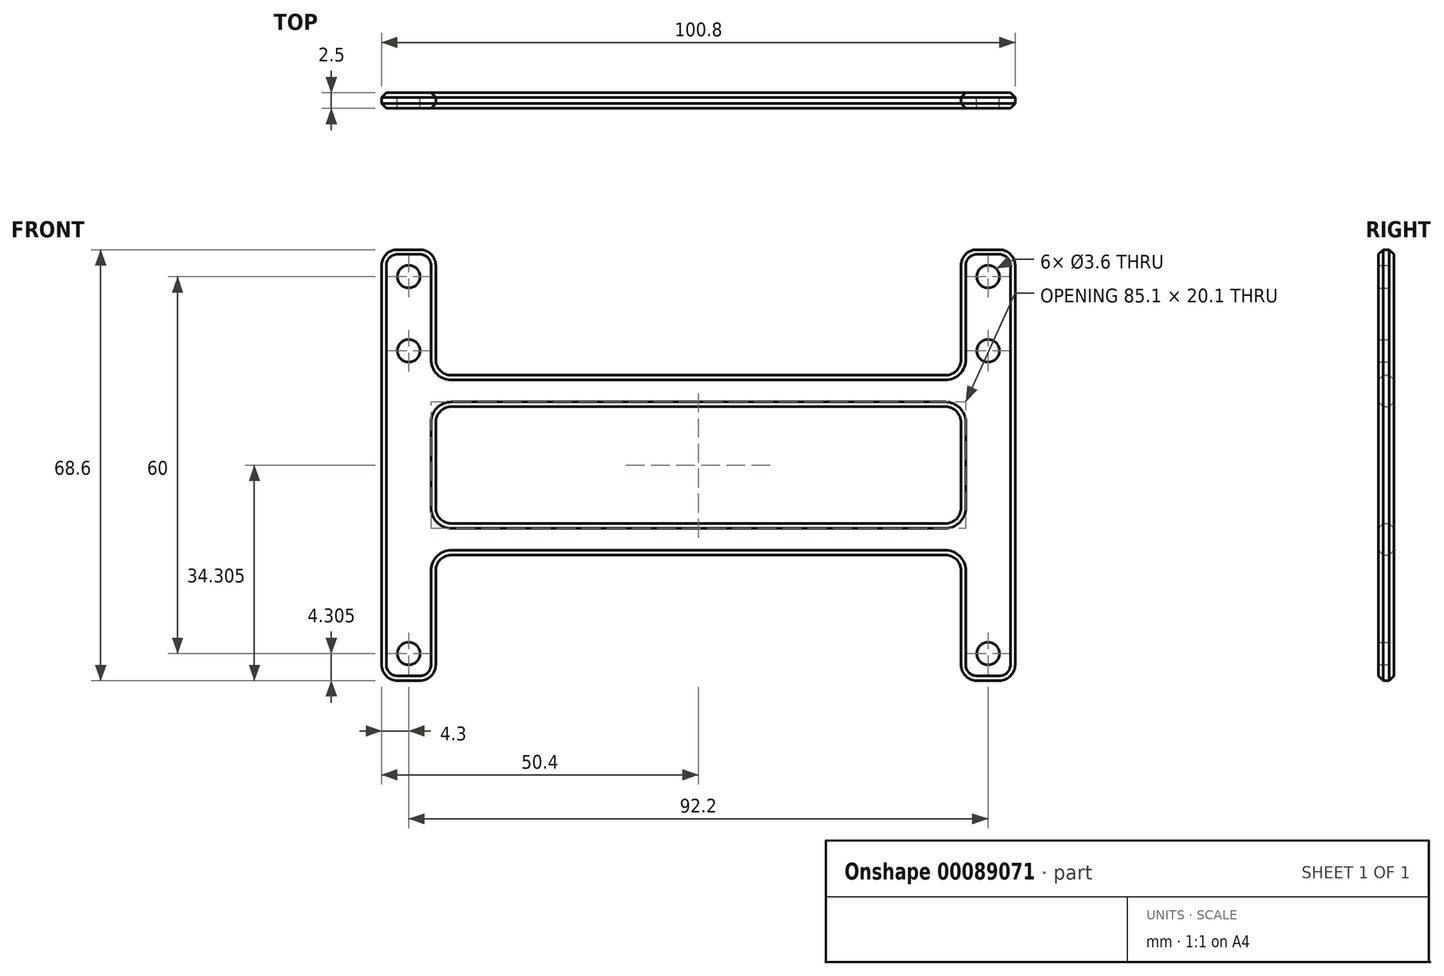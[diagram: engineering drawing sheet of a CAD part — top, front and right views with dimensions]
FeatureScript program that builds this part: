
annotation { "Feature Type Name" : "Feature", "Feature Type Description" : "" }
export const myFeature = defineFeature(function(context is Context, id is Id, definition is map)
    precondition{}
    {
        {
            var Q0;
            Q0=qCreatedBy(makeId("Front.planeOp"),FACE);
            var sketch = newSketch(context, id + "F0", { "sketchPlane" : qUnion([Q0])});
            skLineSegment(sketch, "E0.bottom", {"start": v(-50.4, 64.62) * mm, "end": v(-41.8, 64.62) * mm});
            skLineSegment(sketch, "E0.top", {"start": v(-50.4, -3.98) * mm, "end": v(-41.8, -3.98) * mm});
            skLineSegment(sketch, "E0.left", {"start": v(-50.4, 64.62) * mm, "end": v(-50.4, -3.98) * mm});
            skLineSegment(sketch, "E1", {"start": v(-46.1, 64.62) * mm, "end": v(-46.1, -55.68) * mm, "construction": true});
            skCircle(sketch, "E2", {"center": v(-46.1, 60.32) * mm, "radius": 1.8 * mm});
            skCircle(sketch, "E3", {"center": v(-46.1, 48.52) * mm, "radius": 1.8 * mm});
            skCircle(sketch, "E4", {"center": v(-46.1, 0.32) * mm, "radius": 1.8 * mm});
            skLineSegment(sketch, "E5", {"start": v(-41.8, 64.62) * mm, "end": v(-41.8, -3.98) * mm});
            skLineSegment(sketch, "E6.bottom", {"start": v(-41.8, 44.62) * mm, "end": v(0, 44.62) * mm});
            skLineSegment(sketch, "E6.top", {"start": v(-41.8, 39.62) * mm, "end": v(0, 39.62) * mm});
            skLineSegment(sketch, "E6.left", {"start": v(-41.8, 44.62) * mm, "end": v(-41.8, 39.62) * mm});
            skLineSegment(sketch, "E6.right", {"start": v(0, 44.62) * mm, "end": v(0, 39.62) * mm});
            skLineSegment(sketch, "E7.bottom", {"start": v(-41.83, 21.03) * mm, "end": v(0, 21.02) * mm});
            skLineSegment(sketch, "E7.top", {"start": v(-41.83, 16.03) * mm, "end": v(0, 16.02) * mm});
            skLineSegment(sketch, "E7.left", {"start": v(-41.83, 21.03) * mm, "end": v(-41.83, 16.03) * mm});
            skLineSegment(sketch, "E7.right", {"start": v(0, 21.02) * mm, "end": v(0, 16.02) * mm});
            skLineSegment(sketch, "E8.MirrorCS", {"start": v(41.83, 21.03) * mm, "end": v(41.83, 16.03) * mm});
            skCircle(sketch, "E9.MirrorC", {"center": v(46.1, 48.52) * mm, "radius": 1.8 * mm});
            skLineSegment(sketch, "E10.MirrorCS", {"start": v(41.8, 44.62) * mm, "end": v(41.8, 39.62) * mm});
            skLineSegment(sketch, "E11.MirrorCS", {"start": v(41.83, 16.02) * mm, "end": v(0, 16.02) * mm});
            skLineSegment(sketch, "E12.MirrorCS", {"start": v(41.83, 21.02) * mm, "end": v(0, 21.02) * mm});
            skCircle(sketch, "E13.MirrorC", {"center": v(46.1, 0.32) * mm, "radius": 1.8 * mm});
            skCircle(sketch, "E14.MirrorC", {"center": v(46.1, 60.32) * mm, "radius": 1.8 * mm});
            skLineSegment(sketch, "E15.MirrorCS", {"start": v(41.8, 39.62) * mm, "end": v(0, 39.62) * mm});
            skLineSegment(sketch, "E16.MirrorCS", {"start": v(50.4, 64.62) * mm, "end": v(50.4, -3.98) * mm});
            skLineSegment(sketch, "E17.MirrorCS", {"start": v(50.4, -3.98) * mm, "end": v(41.8, -3.98) * mm});
            skLineSegment(sketch, "E18.MirrorCS", {"start": v(41.8, 64.62) * mm, "end": v(41.8, -3.98) * mm});
            skLineSegment(sketch, "E19.MirrorCS", {"start": v(50.4, 64.62) * mm, "end": v(41.8, 64.62) * mm});
            skLineSegment(sketch, "E20.MirrorCS", {"start": v(41.8, 44.62) * mm, "end": v(0, 44.62) * mm});
            skSolve(sketch);
        }
        {
            var Q0;
            {var subQ5=sQuery(id+"F0.wireOp",EDGE,"E7.left");Q0=makeQuery(id+"F0.imprint","IMPRINT",FACE,{"disambiguationData":[TD([[makeQuery(id+"F0.imprint","IMPRINT",EDGE,{"derivedFrom":subQ5}),1.0]])]});}
            var Q1;
            {var subQ0=sQuery(id+"F0.wireOp",EDGE,"E8.MirrorCS");Q1=makeQuery(id+"F0.imprint","IMPRINT",FACE,{"disambiguationData":[TD([[makeQuery(id+"F0.imprint","IMPRINT",EDGE,{"derivedFrom":subQ0}),-1.0]])]});}
            var Q2;
            {var subQ5=sQuery(id+"F0.wireOp",EDGE,"E7.right");Q2=makeQuery(id+"F0.imprint","IMPRINT",FACE,{"disambiguationData":[TD([[makeQuery(id+"F0.imprint","IMPRINT",EDGE,{"derivedFrom":subQ5}),-1.0]])]});}
            var Q3;
            {var subQ0=sQuery(id+"F0.wireOp",EDGE,"E7.right");Q3=makeQuery(id+"F0.imprint","IMPRINT",FACE,{"disambiguationData":[TD([[makeQuery(id+"F0.imprint","IMPRINT",EDGE,{"derivedFrom":subQ0}),1.0]])]});}
            var Q4;
            {var subQ0=sQuery(id+"F0.wireOp",EDGE,"E15.MirrorCS");Q4=makeQuery(id+"F0.imprint","IMPRINT",FACE,{"disambiguationData":[TD([[makeQuery(id+"F0.imprint","IMPRINT",EDGE,{"derivedFrom":subQ0}),-1.0]])]});}
            var Q5;
            {var subQ9=sQuery(id+"F0.wireOp",EDGE,"E8.MirrorCS");Q5=makeQuery(id+"F0.imprint","IMPRINT",FACE,{"disambiguationData":[TD([[makeQuery(id+"F0.imprint","IMPRINT",EDGE,{"derivedFrom":subQ9}),1.0]])]});}
            var Q6;
            Q6=makeQuery(id+"F0.imprint","IMPRINT",FACE,{"disambiguationData":[TD([[makeQuery(id+"F0.imprint","IMPRINT",EDGE,{"derivedFrom":sQuery(id+"F0.wireOp",EDGE,"E6.bottom")}),-1.0]])]});
            var Q7;
            Q7=makeQuery(id+"F0.imprint","IMPRINT",FACE,{"disambiguationData":[TD([[makeQuery(id+"F0.imprint","IMPRINT",EDGE,{"derivedFrom":sQuery(id+"F0.wireOp",EDGE,"6060c022-7060-453b-8efb-dcd9e4211910.sketch_text.stroke-0")}),-1.0]])]});
            var Q8;
            Q8=makeQuery(id+"F0.imprint","IMPRINT",FACE,{"disambiguationData":[TD([[makeQuery(id+"F0.imprint","IMPRINT",EDGE,{"derivedFrom":sQuery(id+"F0.wireOp",EDGE,"6060c022-7060-453b-8efb-dcd9e4211910.sketch_text.stroke-80")}),-1.0]])]});
            var Q9;
            Q9=makeQuery(id+"F0.imprint","IMPRINT",FACE,{"disambiguationData":[TD([[makeQuery(id+"F0.imprint","IMPRINT",EDGE,{"derivedFrom":sQuery(id+"F0.wireOp",EDGE,"6060c022-7060-453b-8efb-dcd9e4211910.sketch_text.stroke-109")}),1.0]])]});
            var Q10;
            Q10=makeQuery(id+"F0.imprint","IMPRINT",FACE,{"disambiguationData":[TD([[makeQuery(id+"F0.imprint","IMPRINT",EDGE,{"derivedFrom":sQuery(id+"F0.wireOp",EDGE,"6060c022-7060-453b-8efb-dcd9e4211910.sketch_text.stroke-75")}),1.0]])]});
            var Q11;
            Q11=makeQuery(id+"F0.imprint","IMPRINT",FACE,{"disambiguationData":[TD([[makeQuery(id+"F0.imprint","IMPRINT",EDGE,{"derivedFrom":sQuery(id+"F0.wireOp",EDGE,"6060c022-7060-453b-8efb-dcd9e4211910.sketch_text.stroke-56")}),1.0]])]});
            var Q12;
            Q12=makeQuery(id+"F0.imprint","IMPRINT",FACE,{"disambiguationData":[TD([[makeQuery(id+"F0.imprint","IMPRINT",EDGE,{"derivedFrom":sQuery(id+"F0.wireOp",EDGE,"6060c022-7060-453b-8efb-dcd9e4211910.sketch_text.stroke-23")}),-1.0]])]});
            var Q13;
            Q13=makeQuery(id+"F0.imprint","IMPRINT",FACE,{"disambiguationData":[TD([[makeQuery(id+"F0.imprint","IMPRINT",EDGE,{"derivedFrom":sQuery(id+"F0.wireOp",EDGE,"6060c022-7060-453b-8efb-dcd9e4211910.sketch_text.stroke-13")}),-1.0]])]});
            var Q14;
            Q14=makeQuery(id+"F0.imprint","IMPRINT",FACE,{"disambiguationData":[TD([[makeQuery(id+"F0.imprint","IMPRINT",EDGE,{"derivedFrom":sQuery(id+"F0.wireOp",EDGE,"6060c022-7060-453b-8efb-dcd9e4211910.sketch_text.stroke-8")}),1.0]])]});
            var Q15;
            Q15=makeQuery(id+"F0.imprint","IMPRINT",FACE,{"disambiguationData":[TD([[makeQuery(id+"F0.imprint","IMPRINT",EDGE,{"derivedFrom":sQuery(id+"F0.wireOp",EDGE,"6060c022-7060-453b-8efb-dcd9e4211910.sketch_text.stroke-118")}),1.0]])]});
            var Q16;
            Q16=makeQuery(id+"F0.imprint","IMPRINT",FACE,{"disambiguationData":[TD([[makeQuery(id+"F0.imprint","IMPRINT",EDGE,{"derivedFrom":sQuery(id+"F0.wireOp",EDGE,"6060c022-7060-453b-8efb-dcd9e4211910.sketch_text.stroke-136")}),-1.0]])]});
            var Q17;
            Q17=makeQuery(id+"F0.imprint","IMPRINT",FACE,{"disambiguationData":[TD([[makeQuery(id+"F0.imprint","IMPRINT",EDGE,{"derivedFrom":sQuery(id+"F0.wireOp",EDGE,"6060c022-7060-453b-8efb-dcd9e4211910.sketch_text.stroke-124")}),-1.0]])]});
            var Q18;
            Q18=makeQuery(id+"F0.imprint","IMPRINT",FACE,{"disambiguationData":[TD([[makeQuery(id+"F0.imprint","IMPRINT",EDGE,{"derivedFrom":sQuery(id+"F0.wireOp",EDGE,"6060c022-7060-453b-8efb-dcd9e4211910.sketch_text.stroke-42")}),-1.0]])]});
            var Q19;
            Q19=makeQuery(id+"F0.imprint","IMPRINT",FACE,{"disambiguationData":[TD([[makeQuery(id+"F0.imprint","IMPRINT",EDGE,{"derivedFrom":sQuery(id+"F0.wireOp",EDGE,"6060c022-7060-453b-8efb-dcd9e4211910.sketch_text.stroke-187")}),-1.0]])]});
            var Q20;
            Q20=makeQuery(id+"F0.imprint","IMPRINT",FACE,{"disambiguationData":[TD([[makeQuery(id+"F0.imprint","IMPRINT",EDGE,{"derivedFrom":sQuery(id+"F0.wireOp",EDGE,"6060c022-7060-453b-8efb-dcd9e4211910.sketch_text.stroke-61")}),-1.0]])]});
            var Q21;
            {var subQ4=sQuery(id+"F0.wireOp",EDGE,"E0.bottom");Q21=makeQuery(id+"F0.imprint","IMPRINT",FACE,{"disambiguationData":[TD([[makeQuery(id+"F0.imprint","IMPRINT",EDGE,{"derivedFrom":subQ4}),-1.0]])]});}
            var Q22;
            Q22=makeQuery(id+"F0.imprint","IMPRINT",FACE,{"disambiguationData":[TD([[makeQuery(id+"F0.imprint","IMPRINT",EDGE,{"derivedFrom":sQuery(id+"F0.wireOp",EDGE,"6060c022-7060-453b-8efb-dcd9e4211910.sketch_text.stroke-195")}),-1.0]])]});
            var Q23;
            Q23=makeQuery(id+"F0.imprint","IMPRINT",FACE,{"disambiguationData":[TD([[makeQuery(id+"F0.imprint","IMPRINT",EDGE,{"derivedFrom":sQuery(id+"F0.wireOp",EDGE,"6060c022-7060-453b-8efb-dcd9e4211910.sketch_text.stroke-155")}),-1.0]])]});
            var Q24;
            Q24=makeQuery(id+"F0.imprint","IMPRINT",FACE,{"disambiguationData":[TD([[makeQuery(id+"F0.imprint","IMPRINT",EDGE,{"derivedFrom":sQuery(id+"F0.wireOp",EDGE,"6060c022-7060-453b-8efb-dcd9e4211910.sketch_text.stroke-234")}),-1.0]])]});
            var Q25;
            Q25=makeQuery(id+"F0.imprint","IMPRINT",FACE,{"disambiguationData":[TD([[makeQuery(id+"F0.imprint","IMPRINT",EDGE,{"derivedFrom":sQuery(id+"F0.wireOp",EDGE,"6060c022-7060-453b-8efb-dcd9e4211910.sketch_text.stroke-224")}),-1.0]])]});
            var Q26;
            Q26=makeQuery(id+"F0.imprint","IMPRINT",FACE,{"disambiguationData":[TD([[makeQuery(id+"F0.imprint","IMPRINT",EDGE,{"derivedFrom":sQuery(id+"F0.wireOp",EDGE,"6060c022-7060-453b-8efb-dcd9e4211910.sketch_text.stroke-212")}),-1.0]])]});
            var Q27;
            Q27=makeQuery(id+"F0.imprint","IMPRINT",FACE,{"disambiguationData":[TD([[makeQuery(id+"F0.imprint","IMPRINT",EDGE,{"derivedFrom":sQuery(id+"F0.wireOp",EDGE,"6060c022-7060-453b-8efb-dcd9e4211910.sketch_text.stroke-216")}),-1.0]])]});
            var Q28;
            Q28=makeQuery(id+"F0.imprint","IMPRINT",FACE,{"disambiguationData":[TD([[makeQuery(id+"F0.imprint","IMPRINT",EDGE,{"derivedFrom":sQuery(id+"F0.wireOp",EDGE,"6060c022-7060-453b-8efb-dcd9e4211910.sketch_text.stroke-183")}),-1.0]])]});
            var Q29;
            Q29 = qSketchRegion(id + "F0", true);
            extrude(context, id + "F1", {"entities" : qUnion([Q0, Q1, Q2, Q3, Q4, Q5, Q6, Q7, Q8, Q9, Q10, Q11, Q12, Q13, Q14, Q15, Q16, Q17, Q18, Q19, Q20, Q21, Q22, Q23, Q24, Q25, Q26, Q27, Q28, Q29]), "depth" : 2.5 * mm});
        }
        {
            var Q0;
            Q0=makeQuery(id+"F1.opExtrude","SWEPT_EDGE",EDGE,{"disambiguationData":[OSD([sQuery(id+"F0.wireOp",EDGE,"E5"),sQuery(id+"F0.wireOp",EDGE,"E6.bottom"),sQuery(id+"F0.wireOp",EDGE,"E6.left")])]});
            var Q1;
            Q1=makeQuery(id+"F1.opExtrude","SWEPT_EDGE",EDGE,{"disambiguationData":[OSD([sQuery(id+"F0.wireOp",EDGE,"E18.MirrorCS"),sQuery(id+"F0.wireOp",EDGE,"E20.MirrorCS")])]});
            var Q2;
            Q2=makeQuery(id+"F1.opExtrude","SWEPT_EDGE",EDGE,{"disambiguationData":[OSD([sQuery(id+"F0.wireOp",EDGE,"E5"),sQuery(id+"F0.wireOp",EDGE,"E6.top"),sQuery(id+"F0.wireOp",EDGE,"E6.left")])]});
            var Q3;
            Q3=makeQuery(id+"F1.opExtrude","SWEPT_EDGE",EDGE,{"disambiguationData":[OSD([sQuery(id+"F0.wireOp",EDGE,"E15.MirrorCS"),sQuery(id+"F0.wireOp",EDGE,"E18.MirrorCS")])]});
            var Q4;
            Q4=makeQuery(id+"F1.opExtrude","SWEPT_EDGE",EDGE,{"disambiguationData":[OSD([sQuery(id+"F0.wireOp",EDGE,"E5"),sQuery(id+"F0.wireOp",EDGE,"E7.bottom")])]});
            var Q5;
            Q5=makeQuery(id+"F1.opExtrude","SWEPT_EDGE",EDGE,{"disambiguationData":[OSD([sQuery(id+"F0.wireOp",EDGE,"E12.MirrorCS"),sQuery(id+"F0.wireOp",EDGE,"E18.MirrorCS")])]});
            var Q6;
            Q6=makeQuery(id+"F1.opExtrude","SWEPT_EDGE",EDGE,{"disambiguationData":[OSD([sQuery(id+"F0.wireOp",EDGE,"E5"),sQuery(id+"F0.wireOp",EDGE,"E7.top")])]});
            var Q7;
            Q7=makeQuery(id+"F1.opExtrude","SWEPT_EDGE",EDGE,{"disambiguationData":[OSD([sQuery(id+"F0.wireOp",EDGE,"E11.MirrorCS"),sQuery(id+"F0.wireOp",EDGE,"E18.MirrorCS")])]});
            var Q8;
            Q8=makeQuery(id+"F1.opExtrude","SWEPT_EDGE",EDGE,{"disambiguationData":[OSD([sQuery(id+"F0.wireOp",EDGE,"E17.MirrorCS"),sQuery(id+"F0.wireOp",EDGE,"E18.MirrorCS")])]});
            var Q9;
            Q9=makeQuery(id+"F1.opExtrude","SWEPT_EDGE",EDGE,{"disambiguationData":[OSD([sQuery(id+"F0.wireOp",EDGE,"E16.MirrorCS"),sQuery(id+"F0.wireOp",EDGE,"E17.MirrorCS")])]});
            var Q10;
            Q10=makeQuery(id+"F1.opExtrude","SWEPT_EDGE",EDGE,{"disambiguationData":[OSD([sQuery(id+"F0.wireOp",EDGE,"E0.top"),sQuery(id+"F0.wireOp",EDGE,"E0.left")])]});
            var Q11;
            Q11=makeQuery(id+"F1.opExtrude","SWEPT_EDGE",EDGE,{"disambiguationData":[OSD([sQuery(id+"F0.wireOp",EDGE,"E0.top"),sQuery(id+"F0.wireOp",EDGE,"E5")])]});
            var Q12;
            Q12=makeQuery(id+"F1.opExtrude","SWEPT_EDGE",EDGE,{"disambiguationData":[OSD([sQuery(id+"F0.wireOp",EDGE,"E16.MirrorCS"),sQuery(id+"F0.wireOp",EDGE,"E19.MirrorCS")])]});
            var Q13;
            Q13=makeQuery(id+"F1.opExtrude","SWEPT_EDGE",EDGE,{"disambiguationData":[OSD([sQuery(id+"F0.wireOp",EDGE,"E18.MirrorCS"),sQuery(id+"F0.wireOp",EDGE,"E19.MirrorCS")])]});
            var Q14;
            Q14=makeQuery(id+"F1.opExtrude","SWEPT_EDGE",EDGE,{"disambiguationData":[OSD([sQuery(id+"F0.wireOp",EDGE,"E0.bottom"),sQuery(id+"F0.wireOp",EDGE,"E0.left")])]});
            var Q15;
            Q15=makeQuery(id+"F1.opExtrude","SWEPT_EDGE",EDGE,{"disambiguationData":[OSD([sQuery(id+"F0.wireOp",EDGE,"E0.bottom"),sQuery(id+"F0.wireOp",EDGE,"E5")])]});
            fillet(context, id + "F2", {"entities" : qUnion([Q0, Q1, Q2, Q3, Q4, Q5, Q6, Q7, Q8, Q9, Q10, Q11, Q12, Q13, Q14, Q15]), "radius" : 2.5 * mm, "tangentPropagation" : true, "allowEdgeOverflow" : false});
        }
        {
            var Q0;
            Q0=makeQuery(id+"F1.opExtrude","CAP_EDGE",EDGE,{"disambiguationData":[OSD([sQuery(id+"F0.wireOp",EDGE,"E7.top"),sQuery(id+"F0.wireOp",EDGE,"E11.MirrorCS")])],"isStart":true});
            var Q1;
            Q1=makeQuery(id+"F1.opExtrude","CAP_EDGE",EDGE,{"disambiguationData":[OSD([sQuery(id+"F0.wireOp",EDGE,"E6.top"),sQuery(id+"F0.wireOp",EDGE,"E15.MirrorCS")])],"isStart":true});
            var Q2;
            Q2=makeQuery(id+"F1.opExtrude","CAP_EDGE",EDGE,{"disambiguationData":[OSD([sQuery(id+"F0.wireOp",EDGE,"E0.bottom")])],"isStart":false});
            var Q3;
            Q3=makeQuery(id+"F1.opExtrude","CAP_EDGE",EDGE,{"disambiguationData":[OSD([sQuery(id+"F0.wireOp",EDGE,"E6.top"),sQuery(id+"F0.wireOp",EDGE,"E15.MirrorCS")])],"isStart":false});
            chamfer(context, id + "F3", {"entities" : qUnion([Q0, Q1, Q2, Q3]), "width" : .75 * mm, "tangentPropagation" : true});
        }
    });
